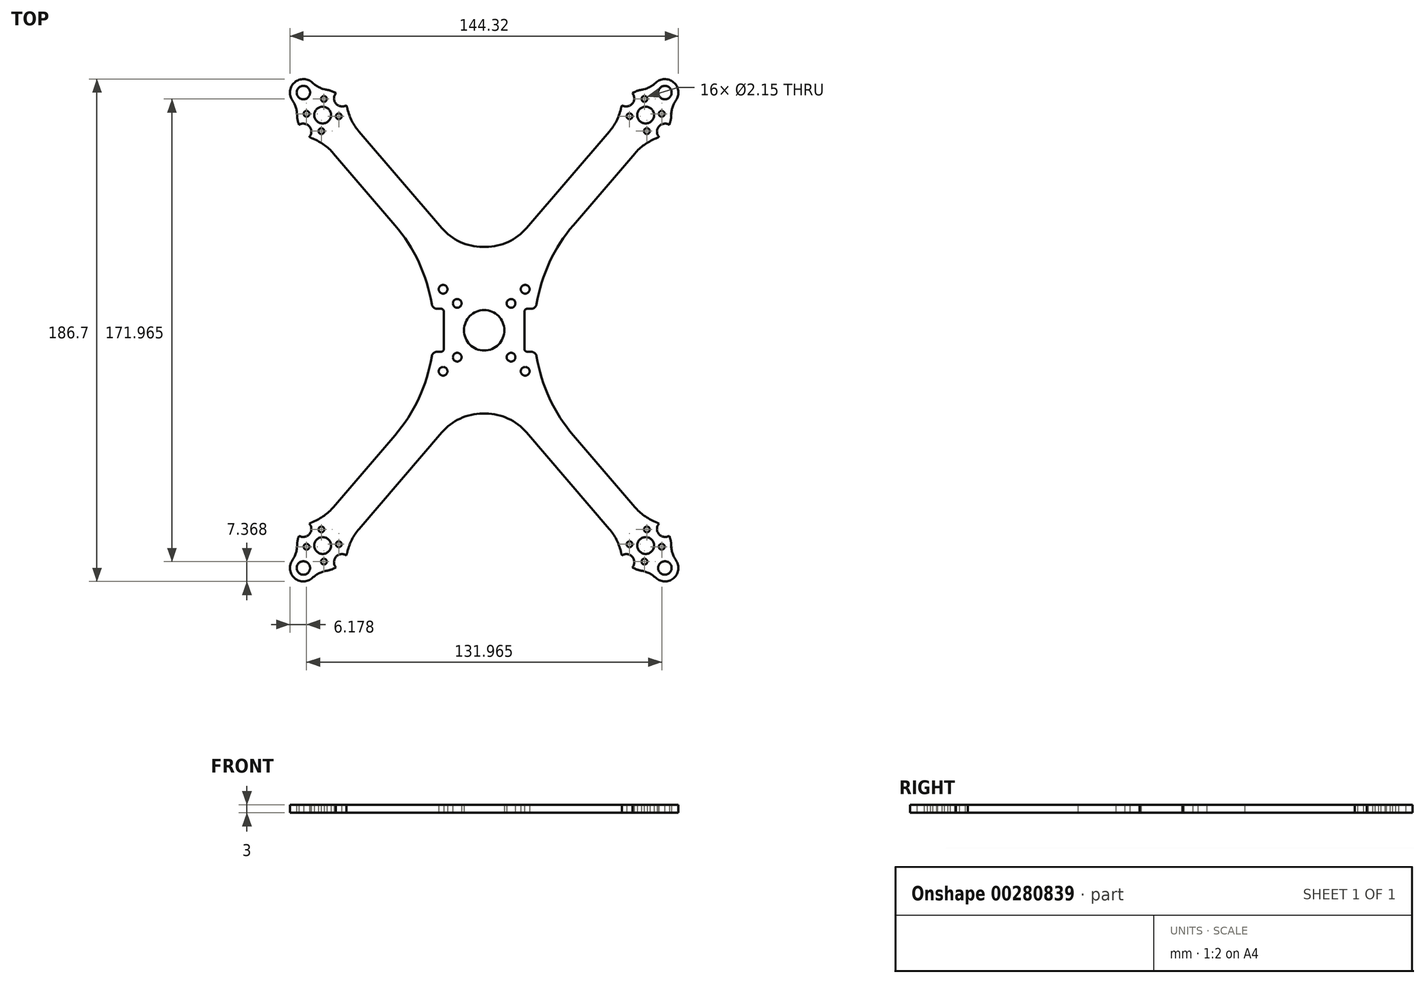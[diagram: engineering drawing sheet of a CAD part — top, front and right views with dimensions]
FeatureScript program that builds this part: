
annotation { "Feature Type Name" : "Feature", "Feature Type Description" : "" }
export const myFeature = defineFeature(function(context is Context, id is Id, definition is map)
    precondition{}
    {
        {
            var Q0;
            Q0=qCreatedBy(makeId("Top.planeOp"),FACE);
            var sketch = newSketch(context, id + "F0", { "sketchPlane" : qUnion([Q0])});
            skLineSegment(sketch, "E0.bottom", {"start": v(-0.57, 31) * mm, "end": v(0.57, 31) * mm});
            skLineSegment(sketch, "E0.top", {"start": v(-0.57, -31) * mm, "end": v(0.57, -31) * mm});
            skLineSegment(sketch, "E1.bottom", {"start": v(-15.25, 15.25) * mm, "end": v(15.25, 15.25) * mm, "construction": true});
            skLineSegment(sketch, "E1.top", {"start": v(-15.25, -15.25) * mm, "end": v(15.25, -15.25) * mm, "construction": true});
            skLineSegment(sketch, "E1.left", {"start": v(-15.25, 15.25) * mm, "end": v(-15.25, -15.25) * mm, "construction": true});
            skLineSegment(sketch, "E1.right", {"start": v(15.25, 15.25) * mm, "end": v(15.25, -15.25) * mm, "construction": true});
            skLineSegment(sketch, "E2.bottom", {"start": v(-10, 10) * mm, "end": v(10, 10) * mm, "construction": true});
            skLineSegment(sketch, "E2.top", {"start": v(-10, -10) * mm, "end": v(10, -10) * mm, "construction": true});
            skLineSegment(sketch, "E2.left", {"start": v(-10, 10) * mm, "end": v(-10, -10) * mm, "construction": true});
            skLineSegment(sketch, "E2.right", {"start": v(10, 10) * mm, "end": v(10, -10) * mm, "construction": true});
            skLineSegment(sketch, "E3", {"start": v(-15.25, 0) * mm, "end": v(15.25, 0) * mm, "construction": true});
            skCircle(sketch, "E4", {"center": v(-15.25, 15.25) * mm, "radius": 1.63 * mm});
            skCircle(sketch, "E5", {"center": v(-10, 10) * mm, "radius": 1.63 * mm});
            skCircle(sketch, "E6", {"center": v(15.25, 15.25) * mm, "radius": 1.63 * mm});
            skCircle(sketch, "E7", {"center": v(10, 10) * mm, "radius": 1.63 * mm});
            skCircle(sketch, "E8.MirrorC", {"center": v(-10, -10) * mm, "radius": 1.63 * mm});
            skCircle(sketch, "E9.MirrorC", {"center": v(-15.25, -15.25) * mm, "radius": 1.63 * mm});
            skCircle(sketch, "E10.MirrorC", {"center": v(15.25, -15.25) * mm, "radius": 1.63 * mm});
            skCircle(sketch, "E11.MirrorC", {"center": v(10, -10) * mm, "radius": 1.63 * mm});
            skCircle(sketch, "E12", {"center": v(0, 0) * mm, "radius": 7.5 * mm});
            skCircle(sketch, "E13", {"center": v(-60, -80) * mm, "radius": 51.3 * mm, "construction": true});
            skLineSegment(sketch, "E14", {"start": v(-18, -31) * mm, "end": v(-60, -80) * mm, "construction": true});
            skCircle(sketch, "E15", {"center": v(-60, -80) * mm, "radius": 6 * mm, "construction": true});
            skCircle(sketch, "E16", {"center": v(-60, -80) * mm, "radius": 3.12 * mm});
            skArc(sketch, "E17", {"start": v(-63.6, -71.2) * mm, "mid": v(-64.27, -71.52) * mm, "end": v(-64.93, -71.88) * mm});
            skLineSegment(sketch, "E18", {"start": v(-33.13, -39.05) * mm, "end": v(-55.99, -65.71) * mm});
            skLineSegment(sketch, "E19", {"start": v(-15.75, -37.98) * mm, "end": v(-46.5, -73.85) * mm});
            skArc(sketch, "E20.filletArc", {"start": v(-33.13, -39.05) * mm, "mid": v(-24.28, -25.3) * mm, "end": v(-19.47, -9.68) * mm});
            skPoint(sketch, "E21.visualSharp", {"position": v(-9.77, -31) * mm});
            skArc(sketch, "E21.filletArc", {"start": v(-0.57, -31) * mm, "mid": v(-8.93, -32.83) * mm, "end": v(-15.75, -37.98) * mm});
            skPoint(sketch, "E22.visualSharp", {"position": v(-60.09, -70.5) * mm});
            skArc(sketch, "E22.filletArc", {"start": v(-63.6, -71.2) * mm, "mid": v(-59.46, -68.91) * mm, "end": v(-55.99, -65.71) * mm});
            skPoint(sketch, "E23.visualSharp", {"position": v(-50.6, -78.64) * mm});
            skArc(sketch, "E23.filletArc", {"start": v(-46.5, -73.85) * mm, "mid": v(-49.13, -77.77) * mm, "end": v(-50.76, -82.21) * mm});
            skArc(sketch, "E24.MirrorCS", {"start": v(-33.13, 39.05) * mm, "mid": v(-24.28, 25.3) * mm, "end": v(-19.47, 9.68) * mm});
            skLineSegment(sketch, "E25.MirrorCS", {"start": v(-33.13, 39.05) * mm, "end": v(-55.99, 65.71) * mm});
            skLineSegment(sketch, "E26.MirrorCS", {"start": v(-15.75, 37.98) * mm, "end": v(-46.5, 73.85) * mm});
            skArc(sketch, "E27.MirrorCS", {"start": v(-0.57, 31) * mm, "mid": v(-8.93, 32.83) * mm, "end": v(-15.75, 37.98) * mm});
            skArc(sketch, "E28.MirrorCS", {"start": v(-63.6, 71.2) * mm, "mid": v(-59.46, 68.91) * mm, "end": v(-55.99, 65.71) * mm});
            skArc(sketch, "E29.MirrorCS", {"start": v(-46.5, 73.85) * mm, "mid": v(-49.13, 77.77) * mm, "end": v(-50.76, 82.21) * mm});
            skCircle(sketch, "E30.MirrorC", {"center": v(-60, 80) * mm, "radius": 3.12 * mm});
            skCircle(sketch, "E31.MirrorC", {"center": v(60, 80) * mm, "radius": 3.12 * mm});
            skArc(sketch, "E32.MirrorCS", {"start": v(46.5, 73.85) * mm, "mid": v(49.13, 77.77) * mm, "end": v(50.76, 82.21) * mm});
            skArc(sketch, "E33.MirrorCS", {"start": v(63.6, 71.2) * mm, "mid": v(59.46, 68.91) * mm, "end": v(55.99, 65.71) * mm});
            skCircle(sketch, "E34.MirrorC", {"center": v(60, -80) * mm, "radius": 3.12 * mm});
            skArc(sketch, "E35.MirrorCS", {"start": v(63.6, -71.2) * mm, "mid": v(59.46, -68.91) * mm, "end": v(55.99, -65.71) * mm});
            skArc(sketch, "E36.MirrorCS", {"start": v(46.5, -73.85) * mm, "mid": v(49.13, -77.77) * mm, "end": v(50.76, -82.21) * mm});
            skPoint(sketch, "E37.MirrorP", {"position": v(60.09, -70.5) * mm});
            skCircle(sketch, "E38.MirrorC", {"center": v(60, -80) * mm, "radius": 6 * mm, "construction": true});
            skPoint(sketch, "E39.MirrorP", {"position": v(50.6, -78.64) * mm});
            skLineSegment(sketch, "E40.MirrorCS", {"start": v(15.75, -37.98) * mm, "end": v(46.5, -73.85) * mm});
            skLineSegment(sketch, "E41.MirrorCS", {"start": v(33.13, -39.05) * mm, "end": v(55.99, -65.71) * mm});
            skLineSegment(sketch, "E42.MirrorCS", {"start": v(15.75, 37.98) * mm, "end": v(46.5, 73.85) * mm});
            skLineSegment(sketch, "E43.MirrorCS", {"start": v(33.13, 39.05) * mm, "end": v(55.99, 65.71) * mm});
            skArc(sketch, "E44.MirrorCS", {"start": v(0.57, 31) * mm, "mid": v(8.93, 32.83) * mm, "end": v(15.75, 37.98) * mm});
            skArc(sketch, "E45.MirrorCS", {"start": v(33.13, 39.05) * mm, "mid": v(24.28, 25.3) * mm, "end": v(19.47, 9.68) * mm});
            skArc(sketch, "E46.MirrorCS", {"start": v(0.57, -31) * mm, "mid": v(8.93, -32.83) * mm, "end": v(15.75, -37.98) * mm});
            skArc(sketch, "E47.MirrorCS", {"start": v(33.13, -39.05) * mm, "mid": v(24.28, -25.3) * mm, "end": v(19.47, -9.68) * mm});
            skLineSegment(sketch, "E48", {"start": v(-60, -80) * mm, "end": v(-60.46, -74.02) * mm, "construction": true});
            skCircle(sketch, "E49", {"center": v(-60.46, -74.02) * mm, "radius": 1.07 * mm});
            skCircle(sketch, "E50.1.0", {"center": v(-65.98, -80.46) * mm, "radius": 1.07 * mm});
            skCircle(sketch, "E50.2.0", {"center": v(-59.54, -85.98) * mm, "radius": 1.07 * mm});
            skCircle(sketch, "E50.3.0", {"center": v(-54.02, -79.54) * mm, "radius": 1.07 * mm});
            skArc(sketch, "E51", {"start": v(-51.22, -83.63) * mm, "mid": v(-55.06, -84.23) * mm, "end": v(-55.07, -88.12) * mm});
            skLineSegment(sketch, "E52", {"start": v(-60, -80) * mm, "end": v(-52.79, -86.18) * mm, "construction": true});
            skArc(sketch, "E53.trimOffspring", {"start": v(-51.22, -83.63) * mm, "mid": v(-50.96, -82.93) * mm, "end": v(-50.76, -82.21) * mm});
            skArc(sketch, "E54.MirrorCS", {"start": v(-64.93, -71.88) * mm, "mid": v(-64.94, -75.77) * mm, "end": v(-68.78, -76.37) * mm});
            skArc(sketch, "E55.trimOffspring", {"start": v(-68.78, -76.37) * mm, "mid": v(-69.31, -78.11) * mm, "end": v(-69.5, -79.91) * mm});
            skLineSegment(sketch, "E56", {"start": v(-60, -80) * mm, "end": v(-67.16, -88.35) * mm, "construction": true});
            skCircle(sketch, "E57", {"center": v(-67.16, -88.35) * mm, "radius": 2.5 * mm});
            skArc(sketch, "E58", {"start": v(-71.27, -85.5) * mm, "mid": v(-70.41, -92.15) * mm, "end": v(-63.72, -91.98) * mm});
            skArc(sketch, "E59.trimOffspring", {"start": v(-58.46, -89.37) * mm, "mid": v(-56.7, -88.91) * mm, "end": v(-55.07, -88.12) * mm});
            skPoint(sketch, "E60.visualSharp", {"position": v(-62.24, -89.23) * mm});
            skArc(sketch, "E60.filletArc", {"start": v(-58.46, -89.37) * mm, "mid": v(-61.29, -90.28) * mm, "end": v(-63.72, -91.98) * mm});
            skPoint(sketch, "E61.visualSharp", {"position": v(-68.78, -83.62) * mm});
            skArc(sketch, "E61.filletArc", {"start": v(-71.27, -85.5) * mm, "mid": v(-69.97, -82.84) * mm, "end": v(-69.5, -79.91) * mm});
            skPoint(sketch, "E62.MirrorP", {"position": v(68.78, -83.62) * mm});
            skCircle(sketch, "E63.MirrorC", {"center": v(67.16, -88.35) * mm, "radius": 2.5 * mm});
            skArc(sketch, "E64.MirrorCS", {"start": v(68.78, -76.37) * mm, "mid": v(69.31, -78.11) * mm, "end": v(69.5, -79.91) * mm});
            skCircle(sketch, "E65.MirrorC", {"center": v(65.98, -80.46) * mm, "radius": 1.07 * mm});
            skArc(sketch, "E66.MirrorCS", {"start": v(71.27, -85.5) * mm, "mid": v(69.97, -82.84) * mm, "end": v(69.5, -79.91) * mm});
            skArc(sketch, "E67.MirrorCS", {"start": v(64.93, -71.88) * mm, "mid": v(64.94, -75.77) * mm, "end": v(68.78, -76.37) * mm});
            skArc(sketch, "E68.MirrorCS", {"start": v(58.46, -89.37) * mm, "mid": v(61.29, -90.28) * mm, "end": v(63.72, -91.98) * mm});
            skArc(sketch, "E69.MirrorCS", {"start": v(58.46, -89.37) * mm, "mid": v(56.7, -88.91) * mm, "end": v(55.07, -88.12) * mm});
            skArc(sketch, "E70.MirrorCS", {"start": v(51.22, -83.63) * mm, "mid": v(55.06, -84.23) * mm, "end": v(55.07, -88.12) * mm});
            skArc(sketch, "E71.MirrorCS", {"start": v(63.6, -71.2) * mm, "mid": v(64.27, -71.52) * mm, "end": v(64.93, -71.88) * mm});
            skArc(sketch, "E72.MirrorCS", {"start": v(51.22, -83.63) * mm, "mid": v(50.96, -82.93) * mm, "end": v(50.76, -82.21) * mm});
            skCircle(sketch, "E73.MirrorC", {"center": v(54.02, -79.54) * mm, "radius": 1.07 * mm});
            skCircle(sketch, "E74.MirrorC", {"center": v(59.54, -85.98) * mm, "radius": 1.07 * mm});
            skCircle(sketch, "E75.MirrorC", {"center": v(60.46, -74.02) * mm, "radius": 1.07 * mm});
            skArc(sketch, "E76.MirrorCS", {"start": v(71.27, -85.5) * mm, "mid": v(70.41, -92.15) * mm, "end": v(63.72, -91.98) * mm});
            skCircle(sketch, "E77.MirrorC", {"center": v(60.46, 74.02) * mm, "radius": 1.07 * mm});
            skCircle(sketch, "E78.MirrorC", {"center": v(54.02, 79.54) * mm, "radius": 1.07 * mm});
            skArc(sketch, "E79.MirrorCS", {"start": v(51.22, 83.63) * mm, "mid": v(50.96, 82.93) * mm, "end": v(50.76, 82.21) * mm});
            skArc(sketch, "E80.MirrorCS", {"start": v(51.22, 83.63) * mm, "mid": v(55.06, 84.23) * mm, "end": v(55.07, 88.12) * mm});
            skCircle(sketch, "E81.MirrorC", {"center": v(59.54, 85.98) * mm, "radius": 1.07 * mm});
            skArc(sketch, "E82.MirrorCS", {"start": v(58.46, 89.37) * mm, "mid": v(56.7, 88.91) * mm, "end": v(55.07, 88.12) * mm});
            skCircle(sketch, "E83.MirrorC", {"center": v(65.98, 80.46) * mm, "radius": 1.07 * mm});
            skArc(sketch, "E84.MirrorCS", {"start": v(64.93, 71.88) * mm, "mid": v(64.94, 75.77) * mm, "end": v(68.78, 76.37) * mm});
            skArc(sketch, "E85.MirrorCS", {"start": v(68.78, 76.37) * mm, "mid": v(69.31, 78.11) * mm, "end": v(69.5, 79.91) * mm});
            skArc(sketch, "E86.MirrorCS", {"start": v(71.27, 85.5) * mm, "mid": v(69.97, 82.84) * mm, "end": v(69.5, 79.91) * mm});
            skArc(sketch, "E87.MirrorCS", {"start": v(58.46, 89.37) * mm, "mid": v(61.29, 90.28) * mm, "end": v(63.72, 91.98) * mm});
            skArc(sketch, "E88.MirrorCS", {"start": v(71.27, 85.5) * mm, "mid": v(70.41, 92.15) * mm, "end": v(63.72, 91.98) * mm});
            skCircle(sketch, "E89.MirrorC", {"center": v(67.16, 88.35) * mm, "radius": 2.5 * mm});
            skArc(sketch, "E90.MirrorCS", {"start": v(63.6, 71.2) * mm, "mid": v(64.27, 71.52) * mm, "end": v(64.93, 71.88) * mm});
            skCircle(sketch, "E91.MirrorC", {"center": v(-60.46, 74.02) * mm, "radius": 1.07 * mm});
            skCircle(sketch, "E92.MirrorC", {"center": v(-54.02, 79.54) * mm, "radius": 1.07 * mm});
            skCircle(sketch, "E93.MirrorC", {"center": v(-59.54, 85.98) * mm, "radius": 1.07 * mm});
            skCircle(sketch, "E94.MirrorC", {"center": v(-65.98, 80.46) * mm, "radius": 1.07 * mm});
            skArc(sketch, "E95.MirrorCS", {"start": v(-63.6, 71.2) * mm, "mid": v(-64.27, 71.52) * mm, "end": v(-64.93, 71.88) * mm});
            skArc(sketch, "E96.MirrorCS", {"start": v(-51.22, 83.63) * mm, "mid": v(-50.96, 82.93) * mm, "end": v(-50.76, 82.21) * mm});
            skArc(sketch, "E97.MirrorCS", {"start": v(-51.22, 83.63) * mm, "mid": v(-55.06, 84.23) * mm, "end": v(-55.07, 88.12) * mm});
            skArc(sketch, "E98.MirrorCS", {"start": v(-64.93, 71.88) * mm, "mid": v(-64.94, 75.77) * mm, "end": v(-68.78, 76.37) * mm});
            skArc(sketch, "E99.MirrorCS", {"start": v(-68.78, 76.37) * mm, "mid": v(-69.31, 78.11) * mm, "end": v(-69.5, 79.91) * mm});
            skArc(sketch, "E100.MirrorCS", {"start": v(-58.46, 89.37) * mm, "mid": v(-56.7, 88.91) * mm, "end": v(-55.07, 88.12) * mm});
            skArc(sketch, "E101.MirrorCS", {"start": v(-58.46, 89.37) * mm, "mid": v(-61.29, 90.28) * mm, "end": v(-63.72, 91.98) * mm});
            skArc(sketch, "E102.MirrorCS", {"start": v(-71.27, 85.5) * mm, "mid": v(-70.41, 92.15) * mm, "end": v(-63.72, 91.98) * mm});
            skArc(sketch, "E103.MirrorCS", {"start": v(-71.27, 85.5) * mm, "mid": v(-69.97, 82.84) * mm, "end": v(-69.5, 79.91) * mm});
            skCircle(sketch, "E104.MirrorC", {"center": v(-67.16, 88.35) * mm, "radius": 2.5 * mm});
            skLineSegment(sketch, "E105", {"start": v(-15, 7) * mm, "end": v(-15, -7) * mm});
            skLineSegment(sketch, "E106", {"start": v(-16, 8) * mm, "end": v(-17.5, 8) * mm});
            skLineSegment(sketch, "E107", {"start": v(-16, -8) * mm, "end": v(-17.5, -8) * mm});
            skPoint(sketch, "E108.visualSharp", {"position": v(-15, 8) * mm});
            skArc(sketch, "E108.filletArc", {"start": v(-15, 7) * mm, "mid": v(-15.3, 7.7) * mm, "end": v(-16, 8) * mm});
            skPoint(sketch, "E109.visualSharp", {"position": v(-15, -8) * mm});
            skArc(sketch, "E109.filletArc", {"start": v(-16, -8) * mm, "mid": v(-15.3, -7.7) * mm, "end": v(-15, -7) * mm});
            skLineSegment(sketch, "E110.MirrorCS", {"start": v(16, 8) * mm, "end": v(17.5, 8) * mm});
            skLineSegment(sketch, "E111.MirrorCS", {"start": v(15, 7) * mm, "end": v(15, -7) * mm});
            skLineSegment(sketch, "E112.MirrorCS", {"start": v(16, -8) * mm, "end": v(17.5, -8) * mm});
            skArc(sketch, "E113.MirrorCS", {"start": v(15, 7) * mm, "mid": v(15.3, 7.7) * mm, "end": v(16, 8) * mm});
            skArc(sketch, "E114.MirrorCS", {"start": v(16, -8) * mm, "mid": v(15.3, -7.7) * mm, "end": v(15, -7) * mm});
            skPoint(sketch, "E115.MirrorP", {"position": v(15, -8) * mm});
            skPoint(sketch, "E116.MirrorP", {"position": v(15, 8) * mm});
            skPoint(sketch, "E117.visualSharp", {"position": v(-19.22, 8) * mm});
            skArc(sketch, "E117.filletArc", {"start": v(-19.47, 9.68) * mm, "mid": v(-18.8, 8.48) * mm, "end": v(-17.5, 8) * mm});
            skPoint(sketch, "E118.visualSharp", {"position": v(-19.22, -8) * mm});
            skArc(sketch, "E118.filletArc", {"start": v(-17.5, -8) * mm, "mid": v(-18.8, -8.48) * mm, "end": v(-19.47, -9.68) * mm});
            skPoint(sketch, "E119.visualSharp", {"position": v(19.22, -8) * mm});
            skArc(sketch, "E119.filletArc", {"start": v(19.47, -9.68) * mm, "mid": v(18.8, -8.48) * mm, "end": v(17.5, -8) * mm});
            skPoint(sketch, "E120.visualSharp", {"position": v(19.22, 8) * mm});
            skArc(sketch, "E120.filletArc", {"start": v(17.5, 8) * mm, "mid": v(18.8, 8.48) * mm, "end": v(19.47, 9.68) * mm});
            skSolve(sketch);
        }
        {
            var Q0;
            Q0 = qSketchRegion(id + "F0", true);
            extrude(context, id + "F1", {"entities" : qUnion([Q0]), "depth" : 3 * mm, "offsetDistance" : 25 * mm});
        }
    });
